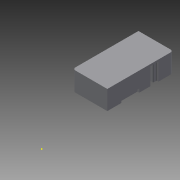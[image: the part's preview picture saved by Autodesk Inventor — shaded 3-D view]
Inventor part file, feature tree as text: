
AUTODESK INVENTOR PART (.ipt)
format: ipt  version: 2015 (Build 190159000, 159)  size: 236,032 bytes
history: native  units: in
note: dims shown in document units (in); Inventor stores cm internally (conversion verified against a paired STEP export)
features: extrude x9, sketch x8, fillet x2, projected_geometry x2, mirror x1
ambient origin geometry x8: Origin, YZ Plane, XZ Plane, XY Plane, X Axis, Y Axis, Z Axis, Center Point
bodies: Solid1 (feature_tree)
feature tree (22):
  extrude  "Extrusion1"  Depth=0.966in
  sketch  "Sketch2"  dims[d5=0.075in d6=0.1in d7=0.1in]
  fillet  "Fillet1"  Radius=0.533in
  fillet  "Fillet2"  Radius=0.075in
  extrude  "Extrusion2"  Depth=0.1in
  extrude  "Extrusion3"  Depth=0.125in
  extrude  "Extrusion4"  Depth=0.1in
  sketch  "Sketch6"  dims[d15=0.1in d16=0.1in]
  extrude  "Extrusion5"  Depth=0.1in
  sketch  "Sketch7"  dims[d17=0.1in d18=0.483in]
  extrude  "Extrusion7"  Depth=0.483in
  extrude  "Extrusion8"  Depth=0.1in
  extrude  "Extrusion9"  Depth=0.1in
  extrude  "Extrusion10"  Depth=0.1in
  mirror  "Mirror1"
  sketch  "Sketch1"  dims[d0=1.833in d1=0.966in d2=0.533in d3=0.0in d4=0.075in]
  sketch  "Sketch4"  dims[d8=0.1in d9=0.1in d11=0.125in]
  sketch  "Sketch5"  dims[d13=0.2in d14=0.1in]
  sketch  "Sketch8"  dims[d19=0.0in d20=0.1in]
  projected_geometry  "Projected Loop1"
  sketch  "Sketch9"  dims[d21=0.24in d22=0.1in d23=0.545in d24=0.5in d25=0.45in d26=0.9in d27=0.533in d28=0.0in d29=0.279in d30=0.185in d32=0.3in d33=0.1in d34=0.533in d35=0.0in d36=0.1718in d37=1.2625in d38=0.025in d39=0.0in d40=0.05in d41=0.1in d42=0.025in d43=0.025in d46=0.05in d47=0.025in d48=0.0in d49=0.025in d50=0.0in d51=0.1in d52=0.5in d53=0.05in d54=0.0in d55=0.1in d56=0.0in]
  projected_geometry  "Projected Loop2"
